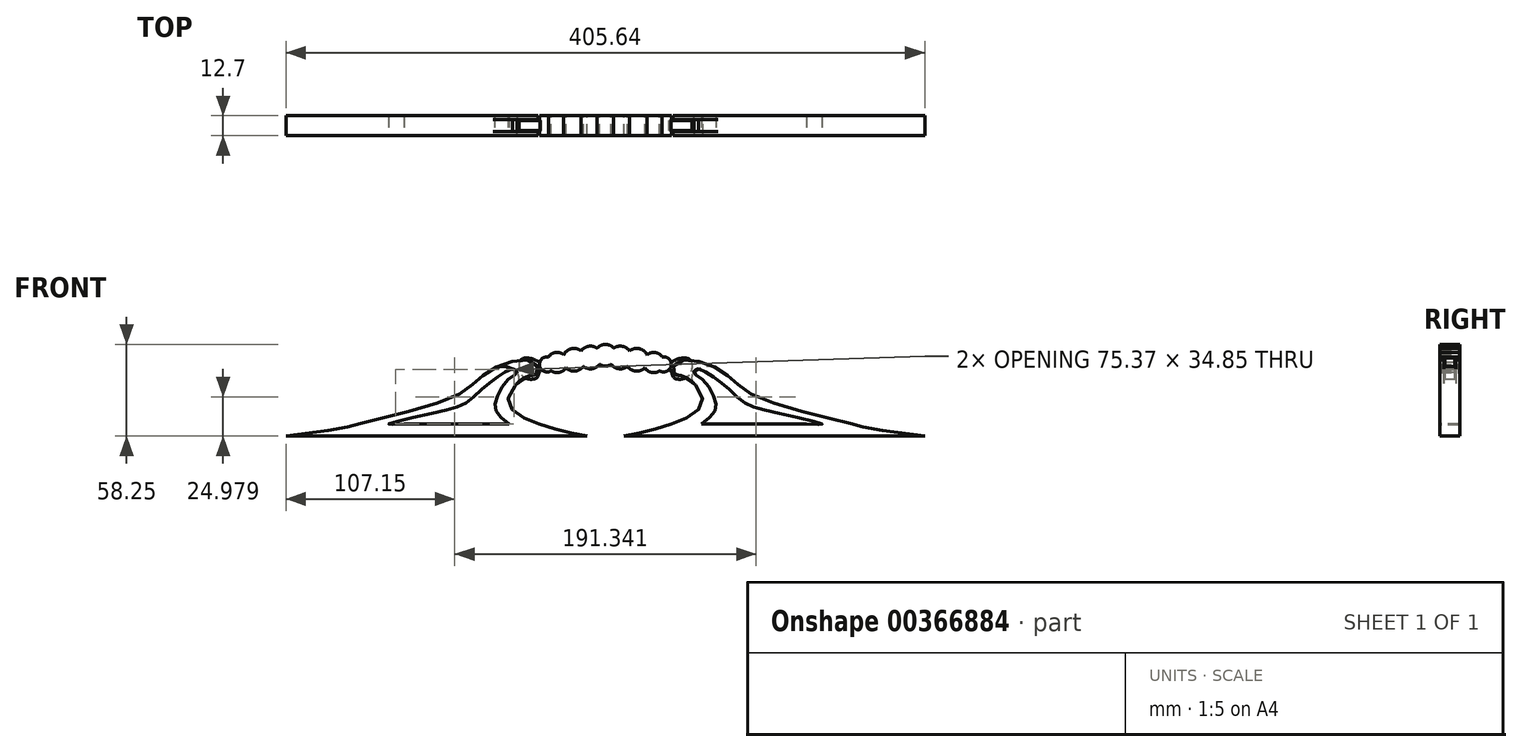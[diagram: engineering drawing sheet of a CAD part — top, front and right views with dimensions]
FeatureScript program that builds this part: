
annotation { "Feature Type Name" : "Feature", "Feature Type Description" : "" }
export const myFeature = defineFeature(function(context is Context, id is Id, definition is map)
    precondition{}
    {
        {
            var Q0;
            Q0=qCreatedBy(makeId("Front.planeOp"),FACE);
            var sketch = newSketch(context, id + "F0", { "sketchPlane" : qUnion([Q0])});
            skLineSegment(sketch, "E0", {"start": v(-202.82, 0) * mm, "end": v(203.58, 0) * mm});
            skFitSpline(sketch, "E1", {"points": [v(-202.82, 0) * mm, v(-153.16, 8.63) * mm, v(-95.12, 25.5) * mm, v(-78.76, 37.65) * mm, v(-60.3, 47.14) * mm, v(-44.47, 46.09) * mm, v(-43.41, 39.76) * mm, v(-50.27, 37.65) * mm, v(-61.88, 23.4) * mm, v(-53.96, 12.85) * mm, v(-33.39, 4.93) * mm, v(-11.75, 0) * mm], "startDerivative": vector(862.98, 105.98) * mm, "endDerivative": vector(232.52, -48.04) * mm});
            skFitSpline(sketch, "E2.MirrorCS", {"points": [v(202.82, 0) * mm, v(153.16, 8.63) * mm, v(95.12, 25.5) * mm, v(78.76, 37.65) * mm, v(60.3, 47.14) * mm, v(44.47, 46.09) * mm, v(43.41, 39.76) * mm, v(50.27, 37.65) * mm, v(61.88, 23.4) * mm, v(53.96, 12.85) * mm, v(33.39, 4.93) * mm, v(11.75, 0) * mm], "startDerivative": vector(-862.98, 105.98) * mm, "endDerivative": vector(-232.52, -48.04) * mm});
            skSolve(sketch);
        }
        {
            var Q0;
            Q0 = qSketchRegion(id + "F0", true);
            extrude(context, id + "F1", {"entities" : qUnion([Q0]), "endBound" : BoundingType.SYMMETRIC, "depth" : 12.7 * mm});
        }
        {
            var Q0;
            Q0=qCreatedBy(makeId("Right.planeOp"),FACE);
            var sketch = newSketch(context, id + "F2", { "sketchPlane" : qUnion([Q0])});
            skLineSegment(sketch, "E3", {"start": v(-3.81, 58.47) * mm, "end": v(-3.8, 25.38) * mm});
            skLineSegment(sketch, "E4", {"start": v(-3.8, 25.38) * mm, "end": v(3.81, 25.38) * mm});
            skLineSegment(sketch, "E5", {"start": v(3.81, 25.38) * mm, "end": v(3.81, 58.47) * mm});
            skLineSegment(sketch, "E6", {"start": v(3.81, 58.47) * mm, "end": v(-3.81, 58.47) * mm});
            skSolve(sketch);
        }
        {
            var Q0;
            Q0 = qSketchRegion(id + "F2", true);
            extrude(context, id + "F3", {"entities" : qUnion([Q0]), "operationType" : NewBodyOperationType.REMOVE, "oppositeDirection" : true, "depth" : 53.34 * mm});
        }
        {
            var Q0;
            Q0 = qSketchRegion(id + "F2", true);
            extrude(context, id + "F4", {"entities" : qUnion([Q0]), "operationType" : NewBodyOperationType.REMOVE, "depth" : 53.34 * mm});
        }
        {
            var Q0;
            Q0=makeQuery(id+"F3.boolean.opBoolean","INTERSECT",EDGE,{"disambiguationData":[OD(1.0)],"derivedFrom":[makeQuery(id+"F1.opExtrude","SWEPT_FACE",FACE,{"disambiguationData":[OSD([sQuery(id+"F0.wireOp",EDGE,"E1")])]}),makeQuery(id+"F3.opExtrude","CAP_FACE",FACE,{"disambiguationData":[OSD([sQuery(id+"F2.wireOp",EDGE,"E3"),sQuery(id+"F2.wireOp",EDGE,"E4"),sQuery(id+"F2.wireOp",EDGE,"E5"),sQuery(id+"F2.wireOp",EDGE,"E6")])],"isStart":false})]});
            var Q1;
            Q1=makeQuery(id+"F4.boolean.opBoolean","INTERSECT",EDGE,{"disambiguationData":[OD(1.0)],"derivedFrom":[makeQuery(id+"F1.opExtrude","SWEPT_FACE",FACE,{"disambiguationData":[OSD([sQuery(id+"F0.wireOp",EDGE,"E2.MirrorCS")])]}),makeQuery(id+"F4.opExtrude","CAP_FACE",FACE,{"disambiguationData":[OSD([sQuery(id+"F2.wireOp",EDGE,"E3"),sQuery(id+"F2.wireOp",EDGE,"E4"),sQuery(id+"F2.wireOp",EDGE,"E5"),sQuery(id+"F2.wireOp",EDGE,"E6")])],"isStart":false})]});
            fillet(context, id + "F5", {"entities" : qUnion([Q0, Q1]), "radius" : 12.7 * mm, "tangentPropagation" : true, "allowEdgeOverflow" : false});
        }
        {
            var Q0;
            {var subQ0=makeQuery(id+"F1.opExtrude","SWEPT_FACE",FACE,{"disambiguationData":[OSD([sQuery(id+"F0.wireOp",EDGE,"E1")])]});Q0=makeQuery(id+"F5.opFillet","BLEND_EDGE",EDGE,{"disambiguationData":[OD(1.0)],"blendedFrom":[makeQuery(id+"F3.boolean.opBoolean","INTERSECT",EDGE,{"disambiguationData":[OD(1.0)],"derivedFrom":[subQ0,makeQuery(id+"F3.opExtrude","CAP_FACE",FACE,{"disambiguationData":[OSD([sQuery(id+"F2.wireOp",EDGE,"E3"),sQuery(id+"F2.wireOp",EDGE,"E4"),sQuery(id+"F2.wireOp",EDGE,"E5"),sQuery(id+"F2.wireOp",EDGE,"E6")])],"isStart":false})]}),subQ0],"blendedInto":[subQ0]});}
            var Q1;
            {var subQ0=makeQuery(id+"F1.opExtrude","SWEPT_FACE",FACE,{"disambiguationData":[OSD([sQuery(id+"F0.wireOp",EDGE,"E2.MirrorCS")])]});Q1=makeQuery(id+"F5.opFillet","BLEND_EDGE",EDGE,{"disambiguationData":[OD(0.0)],"blendedFrom":[makeQuery(id+"F4.boolean.opBoolean","INTERSECT",EDGE,{"disambiguationData":[OD(1.0)],"derivedFrom":[subQ0,makeQuery(id+"F4.opExtrude","CAP_FACE",FACE,{"disambiguationData":[OSD([sQuery(id+"F2.wireOp",EDGE,"E3"),sQuery(id+"F2.wireOp",EDGE,"E4"),sQuery(id+"F2.wireOp",EDGE,"E5"),sQuery(id+"F2.wireOp",EDGE,"E6")])],"isStart":false})]}),subQ0],"blendedInto":[subQ0]});}
            fillet(context, id + "F6", {"entities" : qUnion([Q0, Q1]), "radius" : 5.08 * mm, "tangentPropagation" : true, "allowEdgeOverflow" : false});
        }
        {
            var Q0;
            Q0=qCreatedBy(makeId("Front.planeOp"),FACE);
            var sketch = newSketch(context, id + "F7", { "sketchPlane" : qUnion([Q0])});
            skFitSpline(sketch, "E7", {"points": [v(0, 53.56) * mm, v(-41.56, 47.11) * mm, v(-45.7, 48.8) * mm, v(-52.6, 49.1) * mm, v(-54.91, 45.27) * mm, v(-53.84, 39.6) * mm, v(-50, 36.52) * mm, v(-43.55, 36.98) * mm, v(-41.25, 41.43) * mm, v(0, 49.1) * mm], "startDerivative": vector(-240.64, -49.88) * mm, "endDerivative": vector(250.78, 21.53) * mm});
            skFitSpline(sketch, "E8.MirrorCS", {"points": [v(0, 53.56) * mm, v(41.56, 47.11) * mm, v(45.7, 48.8) * mm, v(52.6, 49.1) * mm, v(54.91, 45.27) * mm, v(53.84, 39.6) * mm, v(50, 36.52) * mm, v(43.55, 36.98) * mm, v(41.25, 41.43) * mm, v(0, 49.1) * mm], "startDerivative": vector(240.64, -49.88) * mm, "endDerivative": vector(-250.78, 21.53) * mm});
            skSolve(sketch);
        }
        {
            var Q0;
            Q0 = qSketchRegion(id + "F7", true);
            extrude(context, id + "F8", {"entities" : qUnion([Q0]), "endBound" : BoundingType.SYMMETRIC, "depth" : 6.35 * mm});
        }
        {
            var Q0;
            Q0=qCreatedBy(makeId("Front.planeOp"),FACE);
            var sketch = newSketch(context, id + "F9", { "sketchPlane" : qUnion([Q0])});
            skCircle(sketch, "E9", {"center": v(0, 51.37) * mm, "radius": 6.88 * mm});
            skCircle(sketch, "E10", {"center": v(-9.44, 49.92) * mm, "radius": 7.23 * mm});
            skCircle(sketch, "E11", {"center": v(-19.91, 48.46) * mm, "radius": 7.23 * mm});
            skCircle(sketch, "E12", {"center": v(-30.68, 46.72) * mm, "radius": 6.46 * mm});
            skCircle(sketch, "E13", {"center": v(-37.03, 45.51) * mm, "radius": 4.8 * mm});
            skCircle(sketch, "E14.MirrorC", {"center": v(9.44, 49.92) * mm, "radius": 7.23 * mm});
            skCircle(sketch, "E15.MirrorC", {"center": v(19.91, 48.46) * mm, "radius": 7.23 * mm});
            skCircle(sketch, "E16.MirrorC", {"center": v(30.68, 46.72) * mm, "radius": 6.46 * mm});
            skCircle(sketch, "E17.MirrorC", {"center": v(37.03, 45.51) * mm, "radius": 4.8 * mm});
            skSolve(sketch);
        }
        {
            var Q0;
            Q0 = qSketchRegion(id + "F9", true);
            extrude(context, id + "F10", {"entities" : qUnion([Q0]), "operationType" : NewBodyOperationType.ADD, "endBound" : BoundingType.SYMMETRIC, "depth" : 12.7 * mm});
        }
        {
            var Q0;
            Q0=qCreatedBy(makeId("Front.planeOp"),FACE);
            var sketch = newSketch(context, id + "F11", { "sketchPlane" : qUnion([Q0])});
            skLineSegment(sketch, "E18", {"start": v(-127.77, 7.55) * mm, "end": v(-61.16, 7.55) * mm});
            skFitSpline(sketch, "E19", {"points": [v(-61.16, 7.55) * mm, v(-69.83, 16.71) * mm, v(-68.84, 24.89) * mm, v(-61.16, 36.52) * mm, v(-56.21, 40.24) * mm, v(-58.2, 42.47) * mm, v(-65.37, 39.74) * mm, v(-77.26, 30.83) * mm, v(-88.9, 20.92) * mm, v(-107.72, 14.98) * mm, v(-137.68, 7.55) * mm, v(-127.77, 7.55) * mm], "startDerivative": vector(-119.98, 97.33) * mm, "endDerivative": vector(186.42, 10.93) * mm});
            skFitSpline(sketch, "E20.MirrorCS", {"points": [v(61.16, 7.55) * mm, v(69.83, 16.71) * mm, v(68.84, 24.89) * mm, v(61.16, 36.52) * mm, v(56.21, 40.24) * mm, v(58.2, 42.47) * mm, v(65.37, 39.74) * mm, v(77.26, 30.83) * mm, v(88.9, 20.92) * mm, v(107.72, 14.98) * mm, v(137.68, 7.55) * mm, v(127.77, 7.55) * mm], "startDerivative": vector(119.98, 97.33) * mm, "endDerivative": vector(-186.42, 10.93) * mm});
            skLineSegment(sketch, "E21.MirrorCS", {"start": v(127.77, 7.55) * mm, "end": v(61.16, 7.55) * mm});
            skSolve(sketch);
        }
        {
            var Q0;
            Q0 = qSketchRegion(id + "F11", true);
            extrude(context, id + "F12", {"entities" : qUnion([Q0]), "operationType" : NewBodyOperationType.REMOVE, "endBound" : BoundingType.SYMMETRIC, "oppositeDirection" : true, "depth" : 25.4 * mm});
        }
    });
